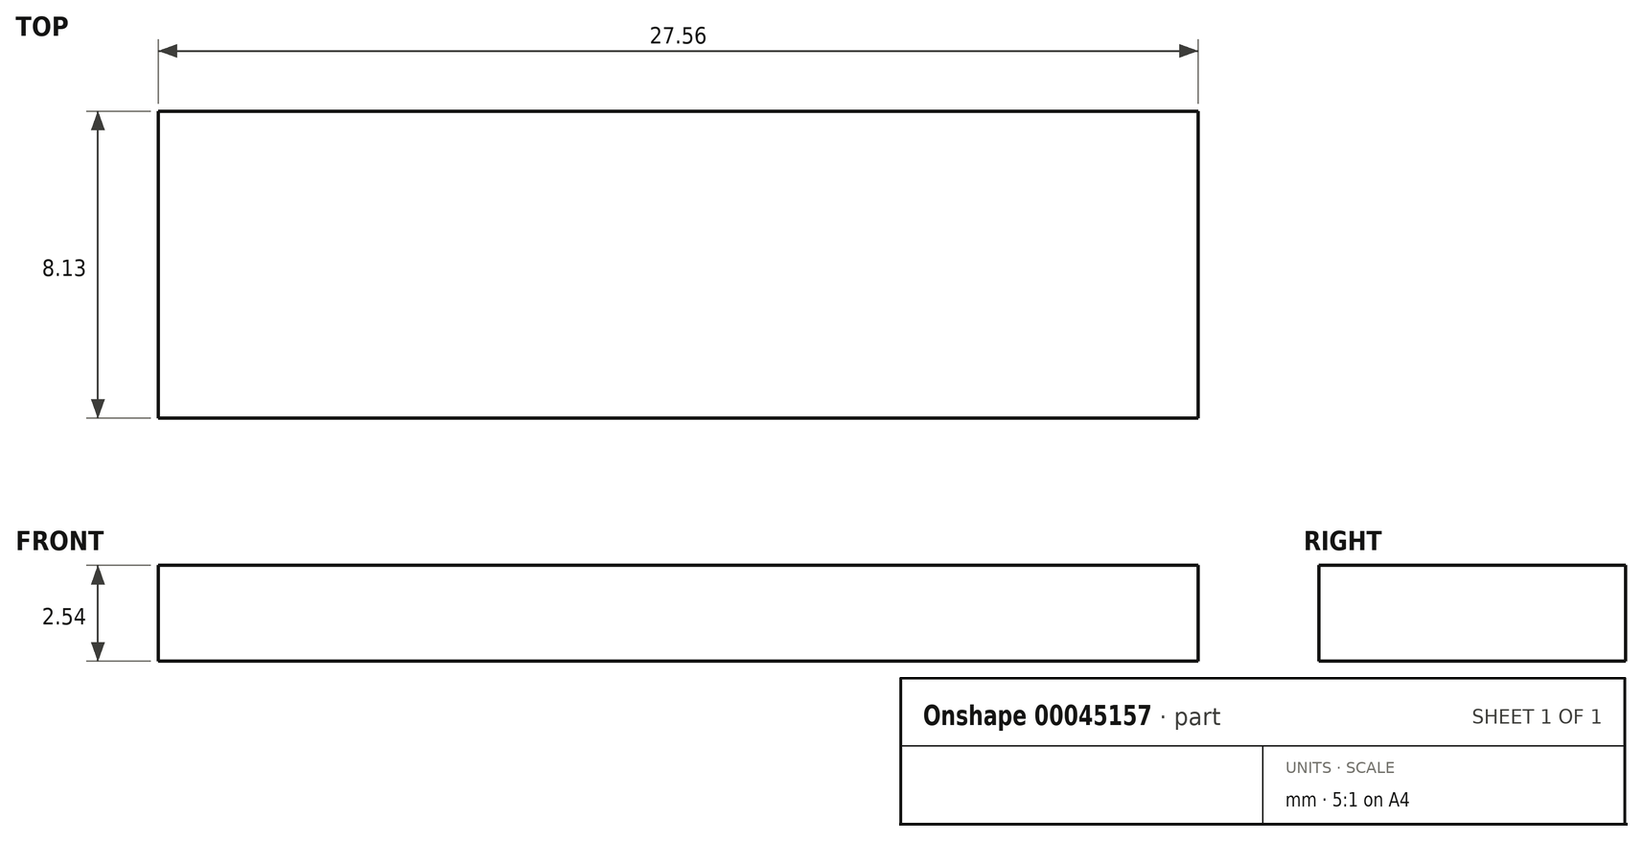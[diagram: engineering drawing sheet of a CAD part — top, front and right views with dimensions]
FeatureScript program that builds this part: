
annotation { "Feature Type Name" : "Feature", "Feature Type Description" : "" }
export const myFeature = defineFeature(function(context is Context, id is Id, definition is map)
    precondition{}
    {
        {
            var Q0;
            Q0=qCreatedBy(makeId("Front.planeOp"),FACE);
            var sketch = newSketch(context, id + "F0", { "sketchPlane" : qUnion([Q0])});
            skLineSegment(sketch, "E0", {"start": v(0, 0) * mm, "end": v(27.56, 0) * mm});
            skLineSegment(sketch, "E1", {"start": v(0, 0) * mm, "end": v(0, 2.54) * mm});
            skLineSegment(sketch, "E2", {"start": v(27.56, 0) * mm, "end": v(27.56, 2.54) * mm});
            skLineSegment(sketch, "E3", {"start": v(0, 2.54) * mm, "end": v(27.56, 2.54) * mm});
            skSolve(sketch);
        }
        {
            var Q0;
            Q0 = qSketchRegion(id + "F0", true);
            extrude(context, id + "F1", {"entities" : qUnion([Q0]), "depth" : 8.13 * mm});
        }
    });
